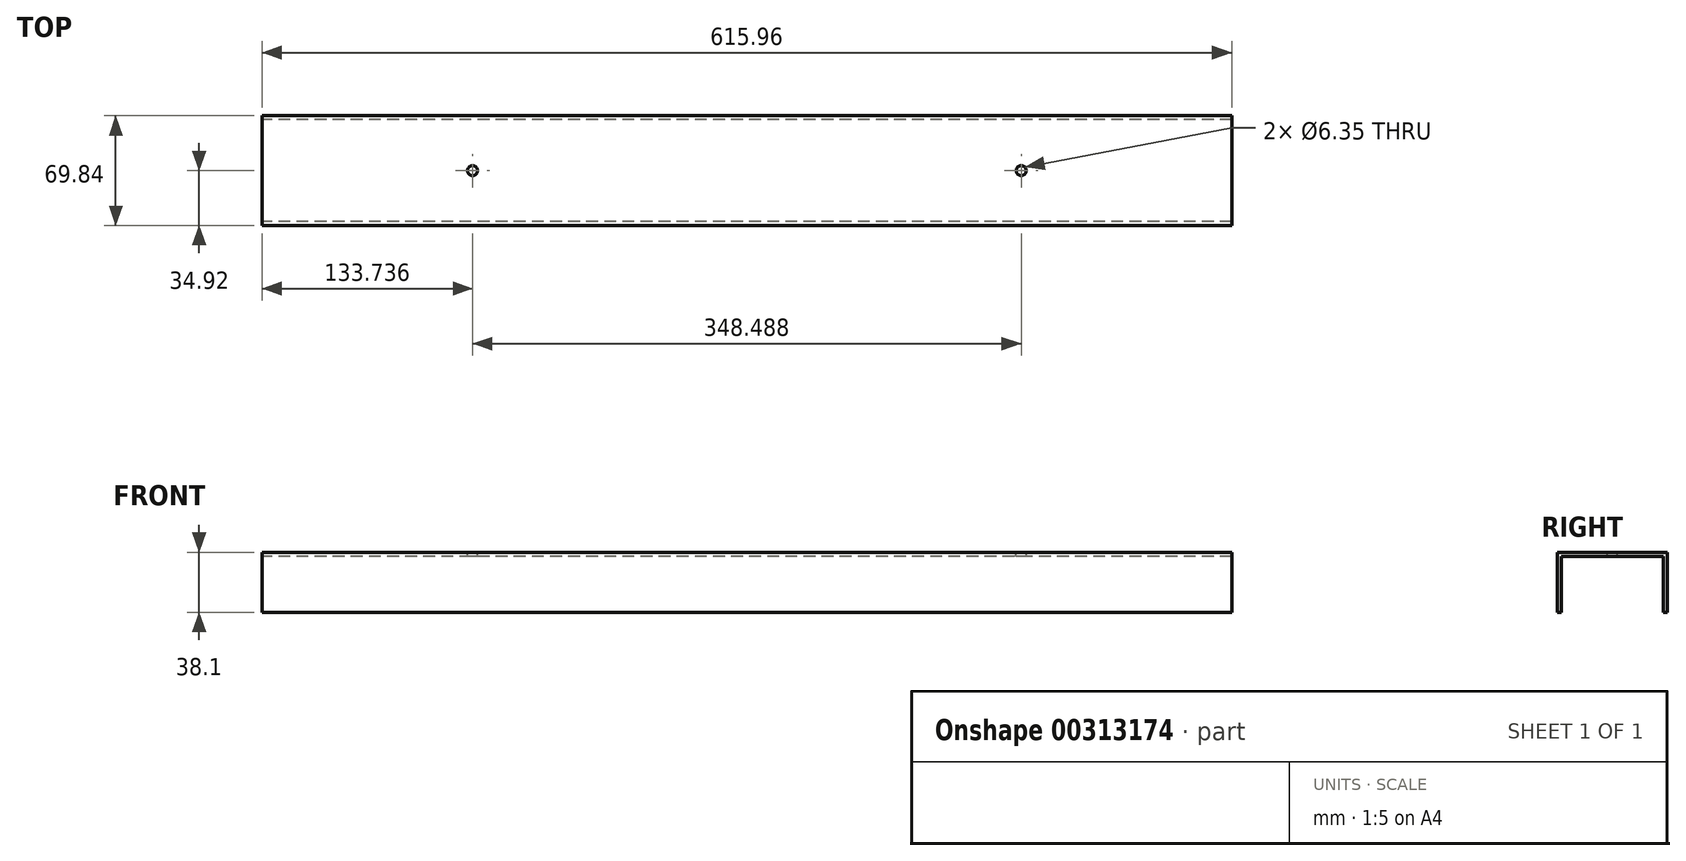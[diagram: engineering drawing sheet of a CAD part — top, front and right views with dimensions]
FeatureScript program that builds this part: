
annotation { "Feature Type Name" : "Feature", "Feature Type Description" : "" }
export const myFeature = defineFeature(function(context is Context, id is Id, definition is map)
    precondition{}
    {
        {
            var Q0;
            Q0=qCreatedBy(makeId("Top.planeOp"),FACE);
            var sketch = newSketch(context, id + "F0", { "sketchPlane" : qUnion([Q0])});
            skLineSegment(sketch, "E0.bottom", {"start": v(307.98, 34.93) * mm, "end": v(-307.98, 34.93) * mm});
            skLineSegment(sketch, "E0.top", {"start": v(307.98, -34.93) * mm, "end": v(-307.98, -34.93) * mm});
            skLineSegment(sketch, "E0.left", {"start": v(307.98, 34.93) * mm, "end": v(307.98, -34.93) * mm});
            skLineSegment(sketch, "E0.right", {"start": v(-307.98, 34.93) * mm, "end": v(-307.98, -34.93) * mm});
            skPoint(sketch, "E0.middle", {"position": v(0, 0) * mm});
            skSolve(sketch);
        }
        {
            var Q0;
            Q0=makeQuery(id+"F0.imprint","IMPRINT",FACE,{"disambiguationData":[TD([[makeQuery(id+"F0.imprint","IMPRINT",EDGE,{"derivedFrom":sQuery(id+"F0.wireOp",EDGE,"E0.bottom")}),1.0]])]});
            extrude(context, id + "F1", {"entities" : qUnion([Q0]), "endBound" : BoundingType.SYMMETRIC, "depth" : 38.1 * mm});
        }
        {
            var Q0;
            Q0=makeQuery(id+"F1.opExtrude","CAP_FACE",FACE,{"disambiguationData":[OSD([sQuery(id+"F0.wireOp",EDGE,"E0.bottom"),sQuery(id+"F0.wireOp",EDGE,"E0.top"),sQuery(id+"F0.wireOp",EDGE,"E0.left"),sQuery(id+"F0.wireOp",EDGE,"E0.right")])],"isStart":true});
            var Q1;
            Q1=makeQuery(id+"F1.opExtrude","SWEPT_FACE",FACE,{"disambiguationData":[OSD([sQuery(id+"F0.wireOp",EDGE,"E0.left")])]});
            var Q2;
            Q2=makeQuery(id+"F1.opExtrude","SWEPT_FACE",FACE,{"disambiguationData":[OSD([sQuery(id+"F0.wireOp",EDGE,"E0.right")])]});
            shell(context, id + "F2", {"entities" : qUnion([Q0, Q1, Q2]), "thickness" : 2.54 * mm});
        }
        {
            var Q0;
            Q0=makeQuery(id+"F1.opExtrude","CAP_FACE",FACE,{"disambiguationData":[OSD([sQuery(id+"F0.wireOp",EDGE,"E0.bottom"),sQuery(id+"F0.wireOp",EDGE,"E0.top"),sQuery(id+"F0.wireOp",EDGE,"E0.left"),sQuery(id+"F0.wireOp",EDGE,"E0.right")])],"isStart":false});
            var sketch = newSketch(context, id + "F3", { "sketchPlane" : qUnion([Q0])});
            skCircle(sketch, "E1", {"center": v(-174.24, 0) * mm, "radius": 3.18 * mm});
            skPoint(sketch, "E1.centerSnap0", {"position": v(-307.98, 0) * mm});
            skCircle(sketch, "E2", {"center": v(174.24, 0) * mm, "radius": 3.18 * mm});
            skLineSegment(sketch, "E3", {"start": v(-174.24, 0) * mm, "end": v(0, 0) * mm, "construction": true});
            skPoint(sketch, "E3.endSnap0", {"position": v(0, -34.93) * mm});
            skLineSegment(sketch, "E4", {"start": v(174.24, 0) * mm, "end": v(0, 0) * mm, "construction": true});
            skSolve(sketch);
        }
        {
            var Q0;
            Q0 = qSketchRegion(id + "F3", true);
            extrude(context, id + "F4", {"entities" : qUnion([Q0]), "operationType" : NewBodyOperationType.REMOVE, "endBound" : BoundingType.THROUGH_ALL, "oppositeDirection" : true, "depth" : 25.4 * mm});
        }
    });
